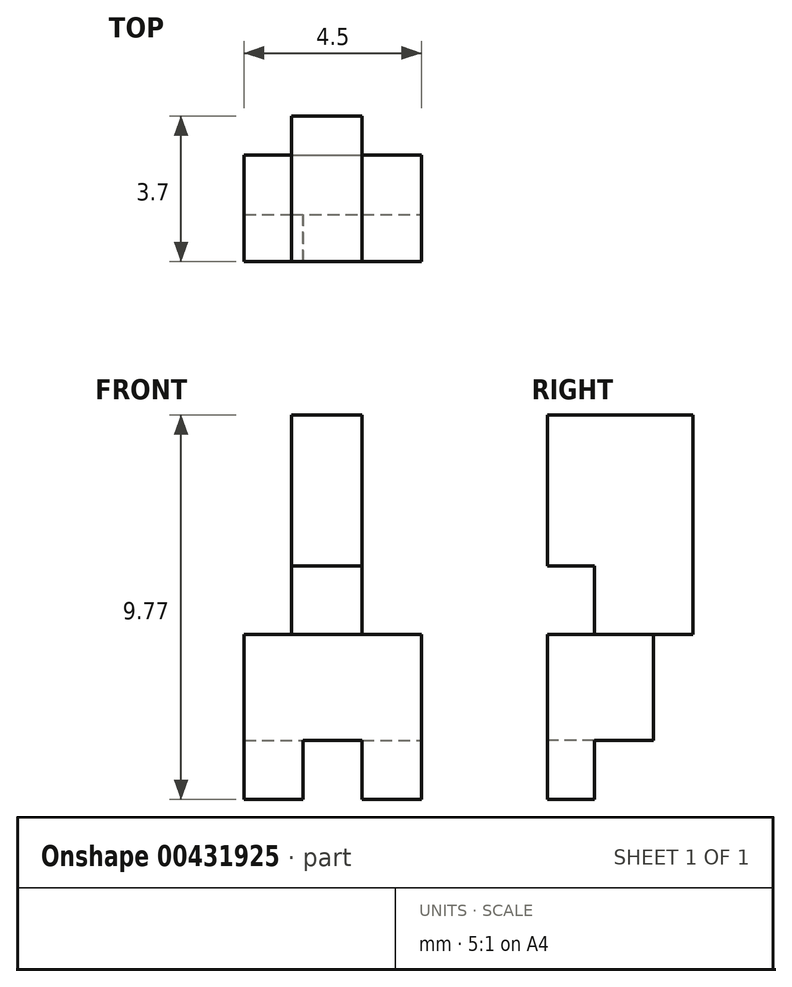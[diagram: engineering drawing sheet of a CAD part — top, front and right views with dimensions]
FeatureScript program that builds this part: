
annotation { "Feature Type Name" : "Feature", "Feature Type Description" : "" }
export const myFeature = defineFeature(function(context is Context, id is Id, definition is map)
    precondition{}
    {
        {
            var Q0;
            Q0=qCreatedBy(makeId("Front.planeOp"),FACE);
            var sketch = newSketch(context, id + "F0", { "sketchPlane" : qUnion([Q0])});
            skLineSegment(sketch, "E0.bottom", {"start": v(-0.75, 0) * mm, "end": v(0.75, 0) * mm});
            skLineSegment(sketch, "E0.top", {"start": v(-0.75, 1.5) * mm, "end": v(0.75, 1.5) * mm});
            skLineSegment(sketch, "E0.left", {"start": v(-0.75, 0) * mm, "end": v(-0.75, 1.5) * mm});
            skLineSegment(sketch, "E0.right", {"start": v(0.75, 0) * mm, "end": v(0.75, 1.5) * mm});
            skLineSegment(sketch, "E1.bottom", {"start": v(-2.25, 0) * mm, "end": v(2.25, 0) * mm});
            skLineSegment(sketch, "E1.top", {"start": v(-2.25, 2.77) * mm, "end": v(2.25, 2.77) * mm});
            skLineSegment(sketch, "E1.left", {"start": v(-2.25, 0) * mm, "end": v(-2.25, 2.77) * mm});
            skLineSegment(sketch, "E1.right", {"start": v(2.25, 0) * mm, "end": v(2.25, 2.77) * mm});
            skLineSegment(sketch, "E2.top", {"start": v(-0.75, 9.77) * mm, "end": v(0.75, 9.77) * mm});
            skLineSegment(sketch, "E2.left", {"start": v(-0.75, 1.5) * mm, "end": v(-0.75, 9.77) * mm});
            skLineSegment(sketch, "E2.right", {"start": v(0.75, 1.5) * mm, "end": v(0.75, 9.77) * mm});
            skLineSegment(sketch, "E3.bottom", {"start": v(-2.25, 1.5) * mm, "end": v(2.25, 1.5) * mm});
            skLineSegment(sketch, "E3.top", {"start": v(-2.25, 4.2) * mm, "end": v(2.25, 4.2) * mm});
            skLineSegment(sketch, "E3.left", {"start": v(-2.25, 1.5) * mm, "end": v(-2.25, 4.2) * mm});
            skLineSegment(sketch, "E3.right", {"start": v(2.25, 1.5) * mm, "end": v(2.25, 4.2) * mm});
            skSolve(sketch);
        }
        {
            var Q0;
            {var subQ2=sQuery(id+"F0.wireOp",EDGE,"E0.left");Q0=makeQuery(id+"F0.imprint","IMPRINT",FACE,{"disambiguationData":[TD([[makeQuery(id+"F0.imprint","IMPRINT",EDGE,{"derivedFrom":subQ2}),1.0]])]});}
            var Q1;
            {var subQ5=sQuery(id+"F0.wireOp",EDGE,"E0.right");Q1=makeQuery(id+"F0.imprint","IMPRINT",FACE,{"disambiguationData":[TD([[makeQuery(id+"F0.imprint","IMPRINT",EDGE,{"derivedFrom":subQ5}),-1.0]])]});}
            var Q2;
            {var subQ5=sQuery(id+"F0.wireOp",EDGE,"E0.top");Q2=makeQuery(id+"F0.imprint","IMPRINT",FACE,{"disambiguationData":[TD([[makeQuery(id+"F0.imprint","IMPRINT",EDGE,{"derivedFrom":subQ5}),1.0]])]});}
            var Q3;
            {var subQ0=sQuery(id+"F0.wireOp",EDGE,"E3.left");var subQ1=sQuery(id+"F0.wireOp",EDGE,"E1.top");var subQ2=makeQuery(id+"F0.imprint","INTERSECT",VERTEX,{"derivedFrom":[subQ1,subQ0]});Q3=makeQuery(id+"F0.imprint","IMPRINT",FACE,{"disambiguationData":[TD([[makeQuery(id+"F0.imprint","IMPRINT",EDGE,{"disambiguationData":[TD([[subQ2,-1.0]])],"derivedFrom":subQ1}),-1.0]])]});}
            var Q4;
            {var subQ0=sQuery(id+"F0.wireOp",EDGE,"E3.left");var subQ1=sQuery(id+"F0.wireOp",EDGE,"E1.top");var subQ2=makeQuery(id+"F0.imprint","INTERSECT",VERTEX,{"derivedFrom":[subQ1,subQ0]});Q4=makeQuery(id+"F0.imprint","IMPRINT",FACE,{"disambiguationData":[TD([[makeQuery(id+"F0.imprint","IMPRINT",EDGE,{"disambiguationData":[TD([[subQ2,-1.0]])],"derivedFrom":subQ1}),1.0]])]});}
            var Q5;
            {var subQ0=sQuery(id+"F0.wireOp",EDGE,"E2.left");var subQ1=sQuery(id+"F0.wireOp",EDGE,"E1.top");var subQ2=makeQuery(id+"F0.imprint","INTERSECT",VERTEX,{"derivedFrom":[subQ1,subQ0]});Q5=makeQuery(id+"F0.imprint","IMPRINT",FACE,{"disambiguationData":[TD([[makeQuery(id+"F0.imprint","IMPRINT",EDGE,{"disambiguationData":[TD([[subQ2,-1.0]])],"derivedFrom":subQ1}),1.0]])]});}
            var Q6;
            {var subQ0=sQuery(id+"F0.wireOp",EDGE,"E3.right");var subQ1=sQuery(id+"F0.wireOp",EDGE,"E1.top");var subQ2=makeQuery(id+"F0.imprint","INTERSECT",VERTEX,{"derivedFrom":[subQ1,subQ0]});Q6=makeQuery(id+"F0.imprint","IMPRINT",FACE,{"disambiguationData":[TD([[makeQuery(id+"F0.imprint","IMPRINT",EDGE,{"disambiguationData":[TD([[subQ2,1.0]])],"derivedFrom":subQ1}),1.0]])]});}
            var Q7;
            {var subQ0=sQuery(id+"F0.wireOp",EDGE,"E3.right");var subQ1=sQuery(id+"F0.wireOp",EDGE,"E1.top");var subQ2=makeQuery(id+"F0.imprint","INTERSECT",VERTEX,{"derivedFrom":[subQ1,subQ0]});Q7=makeQuery(id+"F0.imprint","IMPRINT",FACE,{"disambiguationData":[TD([[makeQuery(id+"F0.imprint","IMPRINT",EDGE,{"disambiguationData":[TD([[subQ2,1.0]])],"derivedFrom":subQ1}),-1.0]])]});}
            var Q8;
            {var subQ0=sQuery(id+"F0.wireOp",EDGE,"E2.left");var subQ1=sQuery(id+"F0.wireOp",EDGE,"E1.top");var subQ2=makeQuery(id+"F0.imprint","INTERSECT",VERTEX,{"derivedFrom":[subQ1,subQ0]});Q8=makeQuery(id+"F0.imprint","IMPRINT",FACE,{"disambiguationData":[TD([[makeQuery(id+"F0.imprint","IMPRINT",EDGE,{"disambiguationData":[TD([[subQ2,-1.0]])],"derivedFrom":subQ1}),-1.0]])]});}
            var Q9;
            {var subQ0=sQuery(id+"F0.wireOp",EDGE,"E2.top");Q9=makeQuery(id+"F0.imprint","IMPRINT",FACE,{"disambiguationData":[TD([[makeQuery(id+"F0.imprint","IMPRINT",EDGE,{"derivedFrom":subQ0}),-1.0]])]});}
            extrude(context, id + "F1", {"entities" : qUnion([Q0, Q1, Q2, Q3, Q4, Q5, Q6, Q7, Q8, Q9]), "depth" : 1.2 * mm});
        }
        {
            var Q0;
            {var subQ0=sQuery(id+"F0.wireOp",EDGE,"E3.right");var subQ1=sQuery(id+"F0.wireOp",EDGE,"E1.top");var subQ2=makeQuery(id+"F0.imprint","INTERSECT",VERTEX,{"derivedFrom":[subQ1,subQ0]});Q0=makeQuery(id+"F0.imprint","IMPRINT",FACE,{"disambiguationData":[TD([[makeQuery(id+"F0.imprint","IMPRINT",EDGE,{"disambiguationData":[TD([[subQ2,1.0]])],"derivedFrom":subQ1}),-1.0]])]});}
            var Q1;
            {var subQ0=sQuery(id+"F0.wireOp",EDGE,"E2.left");var subQ1=sQuery(id+"F0.wireOp",EDGE,"E1.top");var subQ2=makeQuery(id+"F0.imprint","INTERSECT",VERTEX,{"derivedFrom":[subQ1,subQ0]});Q1=makeQuery(id+"F0.imprint","IMPRINT",FACE,{"disambiguationData":[TD([[makeQuery(id+"F0.imprint","IMPRINT",EDGE,{"disambiguationData":[TD([[subQ2,-1.0]])],"derivedFrom":subQ1}),-1.0]])]});}
            var Q2;
            {var subQ0=sQuery(id+"F0.wireOp",EDGE,"E3.left");var subQ1=sQuery(id+"F0.wireOp",EDGE,"E1.top");var subQ2=makeQuery(id+"F0.imprint","INTERSECT",VERTEX,{"derivedFrom":[subQ1,subQ0]});Q2=makeQuery(id+"F0.imprint","IMPRINT",FACE,{"disambiguationData":[TD([[makeQuery(id+"F0.imprint","IMPRINT",EDGE,{"disambiguationData":[TD([[subQ2,-1.0]])],"derivedFrom":subQ1}),-1.0]])]});}
            var Q3;
            {var subQ0=sQuery(id+"F0.wireOp",EDGE,"E3.left");var subQ1=sQuery(id+"F0.wireOp",EDGE,"E1.top");var subQ2=makeQuery(id+"F0.imprint","INTERSECT",VERTEX,{"derivedFrom":[subQ1,subQ0]});Q3=makeQuery(id+"F0.imprint","IMPRINT",FACE,{"disambiguationData":[TD([[makeQuery(id+"F0.imprint","IMPRINT",EDGE,{"disambiguationData":[TD([[subQ2,-1.0]])],"derivedFrom":subQ1}),1.0]])]});}
            var Q4;
            {var subQ0=sQuery(id+"F0.wireOp",EDGE,"E2.left");var subQ1=sQuery(id+"F0.wireOp",EDGE,"E1.top");var subQ2=makeQuery(id+"F0.imprint","INTERSECT",VERTEX,{"derivedFrom":[subQ1,subQ0]});Q4=makeQuery(id+"F0.imprint","IMPRINT",FACE,{"disambiguationData":[TD([[makeQuery(id+"F0.imprint","IMPRINT",EDGE,{"disambiguationData":[TD([[subQ2,-1.0]])],"derivedFrom":subQ1}),1.0]])]});}
            var Q5;
            {var subQ0=sQuery(id+"F0.wireOp",EDGE,"E3.right");var subQ1=sQuery(id+"F0.wireOp",EDGE,"E1.top");var subQ2=makeQuery(id+"F0.imprint","INTERSECT",VERTEX,{"derivedFrom":[subQ1,subQ0]});Q5=makeQuery(id+"F0.imprint","IMPRINT",FACE,{"disambiguationData":[TD([[makeQuery(id+"F0.imprint","IMPRINT",EDGE,{"disambiguationData":[TD([[subQ2,1.0]])],"derivedFrom":subQ1}),1.0]])]});}
            var Q6;
            {var subQ0=sQuery(id+"F0.wireOp",EDGE,"E2.top");Q6=makeQuery(id+"F0.imprint","IMPRINT",FACE,{"disambiguationData":[TD([[makeQuery(id+"F0.imprint","IMPRINT",EDGE,{"derivedFrom":subQ0}),-1.0]])]});}
            extrude(context, id + "F2", {"entities" : qUnion([Q0, Q1, Q2, Q3, Q4, Q5, Q6]), "operationType" : NewBodyOperationType.ADD, "oppositeDirection" : true, "depth" : 1.5 * mm});
        }
        {
            var Q0;
            {var subQ0=sQuery(id+"F0.wireOp",EDGE,"E2.right");Q0=makeQuery(id+"F2.boolean.opBoolean","MERGE",FACE,{"derivedFrom":[makeQuery(id+"F1.opExtrude","SWEPT_FACE",FACE,{"disambiguationData":[OSD([subQ0])]}),makeQuery(id+"F2.opExtrude","SWEPT_FACE",FACE,{"disambiguationData":[OSD([subQ0])]})]});}
            var sketch = newSketch(context, id + "F3", { "sketchPlane" : qUnion([Q0])});
            skLineSegment(sketch, "E4.bottom", {"start": v(-1.2, 4.2) * mm, "end": v(0, 4.2) * mm});
            skLineSegment(sketch, "E4.top", {"start": v(-1.2, 5.94) * mm, "end": v(0, 5.94) * mm});
            skLineSegment(sketch, "E4.left", {"start": v(-1.2, 4.2) * mm, "end": v(-1.2, 5.94) * mm});
            skLineSegment(sketch, "E4.right", {"start": v(0, 4.2) * mm, "end": v(0, 5.94) * mm});
            skSolve(sketch);
        }
        {
            var Q0;
            Q0 = qSketchRegion(id + "F3", true);
            extrude(context, id + "F4", {"entities" : qUnion([Q0]), "operationType" : NewBodyOperationType.REMOVE, "oppositeDirection" : true, "depth" : 2 * mm});
        }
        {
            var Q0;
            Q0=makeQuery(id+"F2.opExtrude","CAP_FACE",FACE,{"disambiguationData":[OSD([sQuery(id+"F0.wireOp",EDGE,"E2.top"),sQuery(id+"F0.wireOp",EDGE,"E2.left"),sQuery(id+"F0.wireOp",EDGE,"E2.right"),sQuery(id+"F0.wireOp",EDGE,"E3.bottom"),sQuery(id+"F0.wireOp",EDGE,"E3.top"),sQuery(id+"F0.wireOp",EDGE,"E3.left"),sQuery(id+"F0.wireOp",EDGE,"E3.right")])],"isStart":false});
            var sketch = newSketch(context, id + "F5", { "sketchPlane" : qUnion([Q0])});
            skLineSegment(sketch, "E5.bottom", {"start": v(0.75, 4.2) * mm, "end": v(-0.75, 4.2) * mm});
            skLineSegment(sketch, "E5.top", {"start": v(0.75, 9.77) * mm, "end": v(-0.75, 9.77) * mm});
            skLineSegment(sketch, "E5.left", {"start": v(0.75, 4.2) * mm, "end": v(0.75, 9.77) * mm});
            skLineSegment(sketch, "E5.right", {"start": v(-0.75, 4.2) * mm, "end": v(-0.75, 9.77) * mm});
            skSolve(sketch);
        }
        {
            var Q0;
            Q0 = qSketchRegion(id + "F5", true);
            extrude(context, id + "F6", {"entities" : qUnion([Q0]), "operationType" : NewBodyOperationType.ADD, "depth" : 1 * mm});
        }
        {
            var Q0;
            {var subQ0=sQuery(id+"F0.wireOp",EDGE,"E2.left");Q0=makeQuery(id+"F6.boolean.opBoolean","MERGE",FACE,{"derivedFrom":[makeQuery(id+"F2.boolean.opBoolean","MERGE",FACE,{"derivedFrom":[makeQuery(id+"F1.opExtrude","SWEPT_FACE",FACE,{"disambiguationData":[OSD([subQ0])]}),makeQuery(id+"F2.opExtrude","SWEPT_FACE",FACE,{"disambiguationData":[OSD([subQ0])]})]}),makeQuery(id+"F6.opExtrude","SWEPT_FACE",FACE,{"disambiguationData":[OSD([sQuery(id+"F5.wireOp",EDGE,"E5.left")])]})]});}
            extrude(context, id + "F7", {"entities" : qUnion([Q0]), "operationType" : NewBodyOperationType.ADD, "depth" : .3 * mm});
        }
    });
